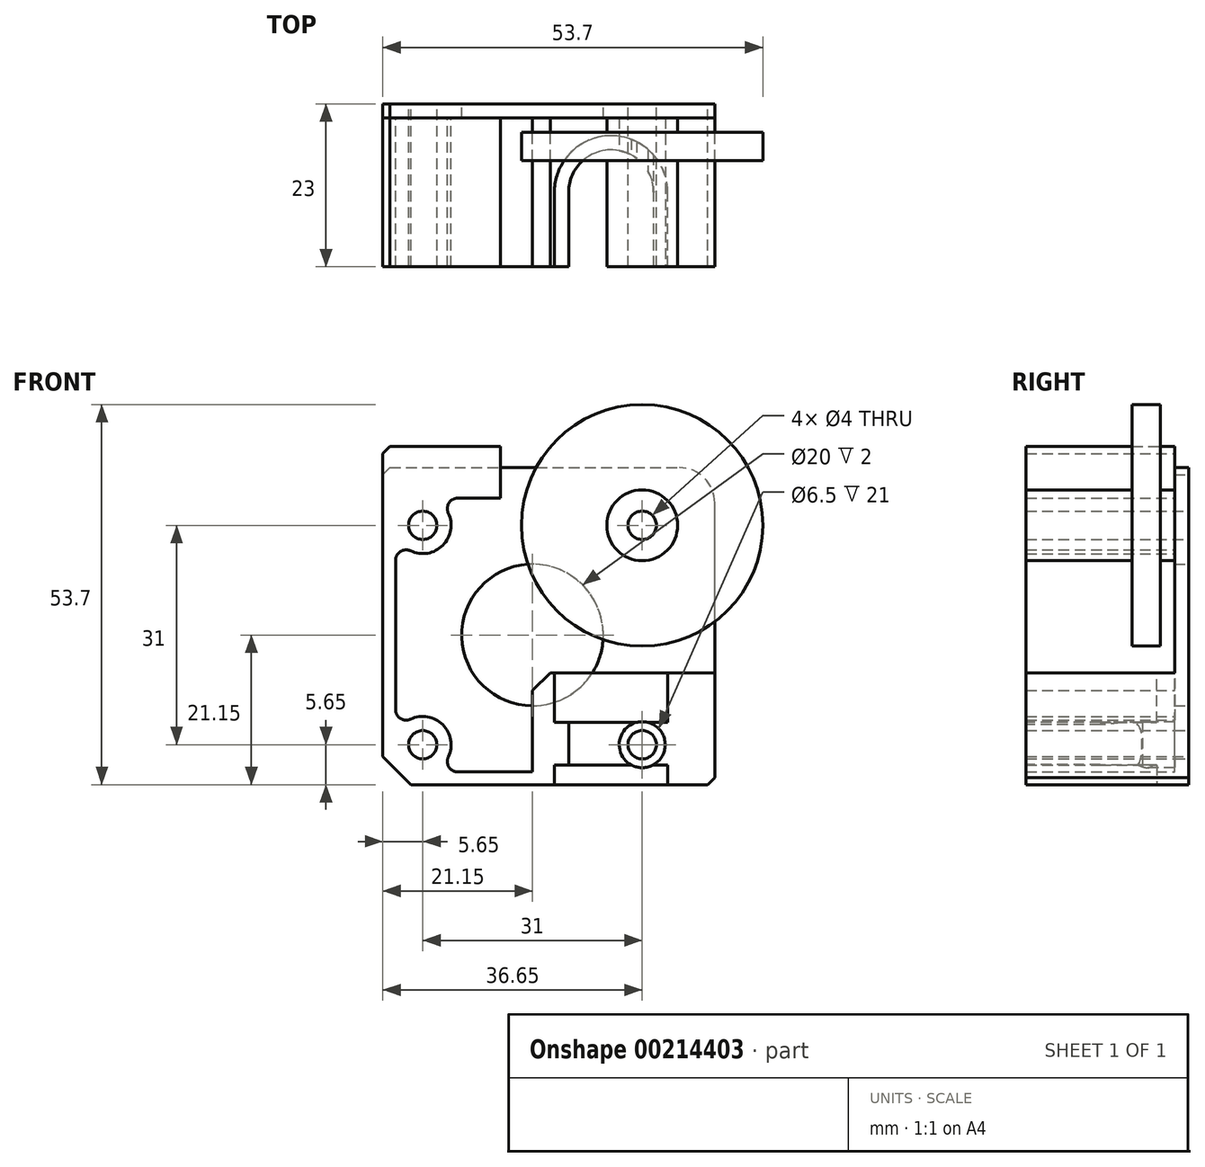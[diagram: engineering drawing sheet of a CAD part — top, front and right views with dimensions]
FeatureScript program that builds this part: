
annotation { "Feature Type Name" : "Feature", "Feature Type Description" : "" }
export const myFeature = defineFeature(function(context is Context, id is Id, definition is map)
    precondition{}
    {
        {
            var Q0;
            Q0=qCreatedBy(makeId("Front.planeOp"),FACE);
            var sketch = newSketch(context, id + "F0", { "sketchPlane" : qUnion([Q0])});
            skLineSegment(sketch, "E0.bottom", {"start": v(4, 0) * mm, "end": v(45.9, 0) * mm});
            skLineSegment(sketch, "E0.top", {"start": v(1, 44.8) * mm, "end": v(41.9, 44.8) * mm});
            skLineSegment(sketch, "E0.left", {"start": v(0, 4) * mm, "end": v(0, 43.8) * mm});
            skLineSegment(sketch, "E0.right", {"start": v(46.9, 1) * mm, "end": v(46.9, 39.8) * mm});
            skLineSegment(sketch, "E1.bottom", {"start": v(4, 0) * mm, "end": v(42.3, 0) * mm, "construction": true});
            skLineSegment(sketch, "E1.top", {"start": v(0, 42.3) * mm, "end": v(42.3, 42.3) * mm, "construction": true});
            skLineSegment(sketch, "E1.left", {"start": v(0, 4) * mm, "end": v(0, 42.3) * mm, "construction": true});
            skLineSegment(sketch, "E1.right", {"start": v(42.3, 0) * mm, "end": v(42.3, 42.3) * mm, "construction": true});
            skLineSegment(sketch, "E2", {"start": v(0, 0) * mm, "end": v(42.3, 42.3) * mm, "construction": true});
            skCircle(sketch, "E3", {"center": v(21.15, 21.15) * mm, "radius": 10 * mm});
            skLineSegment(sketch, "E4", {"start": v(21.15, 42.3) * mm, "end": v(21.15, 0) * mm, "construction": true});
            skCircle(sketch, "E5", {"center": v(36.65, 36.65) * mm, "radius": 2 * mm});
            skCircle(sketch, "E6", {"center": v(5.65, 5.65) * mm, "radius": 2 * mm});
            skLineSegment(sketch, "E7", {"start": v(0, 42.3) * mm, "end": v(42.3, 0) * mm, "construction": true});
            skCircle(sketch, "E8", {"center": v(5.65, 36.65) * mm, "radius": 2 * mm});
            skCircle(sketch, "E9", {"center": v(36.65, 5.65) * mm, "radius": 2 * mm});
            skLineSegment(sketch, "E10", {"start": v(0, 4) * mm, "end": v(4, 0) * mm});
            skLineSegment(sketch, "E11", {"start": v(0, 43.8) * mm, "end": v(1, 44.8) * mm});
            skLineSegment(sketch, "E12", {"start": v(45.9, 0) * mm, "end": v(46.9, 1) * mm});
            skPoint(sketch, "E13.visualSharp", {"position": v(46.9, 44.8) * mm});
            skArc(sketch, "E13.filletArc", {"start": v(46.9, 39.8) * mm, "mid": v(45.44, 43.34) * mm, "end": v(41.9, 44.8) * mm});
            skSolve(sketch);
        }
        {
            var Q0;
            Q0 = qSketchRegion(id + "F0", true);
            extrude(context, id + "F1", {"entities" : qUnion([Q0]), "depth" : 2 * mm});
        }
        {
            var Q0;
            Q0=makeQuery(id+"F1.opExtrude","CAP_FACE",FACE,{"disambiguationData":[OSD([sQuery(id+"F0.wireOp",EDGE,"E0.bottom"),sQuery(id+"F0.wireOp",EDGE,"E0.top"),sQuery(id+"F0.wireOp",EDGE,"E0.left"),sQuery(id+"F0.wireOp",EDGE,"E0.right"),sQuery(id+"F0.wireOp",EDGE,"E3"),sQuery(id+"F0.wireOp",EDGE,"E5"),sQuery(id+"F0.wireOp",EDGE,"E6"),sQuery(id+"F0.wireOp",EDGE,"E8"),sQuery(id+"F0.wireOp",EDGE,"E9"),sQuery(id+"F0.wireOp",EDGE,"E10"),sQuery(id+"F0.wireOp",EDGE,"E11"),sQuery(id+"F0.wireOp",EDGE,"E12"),sQuery(id+"F0.wireOp",EDGE,"E13.filletArc")])],"isStart":false});
            var sketch = newSketch(context, id + "F2", { "sketchPlane" : qUnion([Q0])});
            skLineSegment(sketch, "E14", {"start": v(0, 46.8) * mm, "end": v(0, 4) * mm});
            skLineSegment(sketch, "E15", {"start": v(0, 4) * mm, "end": v(4, 0) * mm});
            skArc(sketch, "E16", {"start": v(9.27, 3.94) * mm, "mid": v(8.48, 8.48) * mm, "end": v(3.94, 9.27) * mm});
            skLineSegment(sketch, "E17.1", {"start": v(10.62, 1.8) * mm, "end": v(21.15, 1.8) * mm});
            skLineSegment(sketch, "E18.trimOffspring", {"start": v(10.62, 40.5) * mm, "end": v(16.65, 40.5) * mm});
            skLineSegment(sketch, "E19.trimOffspring", {"start": v(1.8, 31.68) * mm, "end": v(1.8, 10.62) * mm});
            skArc(sketch, "E20.trimOffspring", {"start": v(3.94, 33.03) * mm, "mid": v(8.48, 33.82) * mm, "end": v(9.27, 38.36) * mm});
            skPoint(sketch, "E21.visualSharp", {"position": v(6.74, 1.8) * mm});
            skArc(sketch, "E21.filletArc", {"start": v(9.27, 3.94) * mm, "mid": v(9.36, 2.5) * mm, "end": v(10.62, 1.8) * mm});
            skPoint(sketch, "E22.visualSharp", {"position": v(1.8, 6.74) * mm});
            skArc(sketch, "E22.filletArc", {"start": v(1.8, 10.62) * mm, "mid": v(2.5, 9.36) * mm, "end": v(3.94, 9.27) * mm});
            skPoint(sketch, "E23.visualSharp", {"position": v(1.8, 35.56) * mm});
            skArc(sketch, "E23.filletArc", {"start": v(3.94, 33.03) * mm, "mid": v(2.5, 32.94) * mm, "end": v(1.8, 31.68) * mm});
            skPoint(sketch, "E24.visualSharp", {"position": v(6.74, 40.5) * mm});
            skArc(sketch, "E24.filletArc", {"start": v(10.62, 40.5) * mm, "mid": v(9.36, 39.8) * mm, "end": v(9.27, 38.36) * mm});
            skLineSegment(sketch, "E25", {"start": v(21.15, 1.8) * mm, "end": v(21.15, 13.3) * mm});
            skLineSegment(sketch, "E26", {"start": v(23.65, 15.8) * mm, "end": v(46.9, 15.8) * mm});
            skLineSegment(sketch, "E27", {"start": v(4, 0) * mm, "end": v(45.9, 0) * mm});
            skLineSegment(sketch, "E28", {"start": v(45.9, 0) * mm, "end": v(46.9, 1) * mm});
            skLineSegment(sketch, "E29", {"start": v(46.9, 1) * mm, "end": v(46.9, 15.8) * mm});
            skLineSegment(sketch, "E30", {"start": v(21.15, 13.3) * mm, "end": v(23.65, 15.8) * mm});
            skLineSegment(sketch, "E31", {"start": v(21.15, 13.3) * mm, "end": v(21.15, 21.15) * mm, "construction": true});
            skLineSegment(sketch, "E32", {"start": v(16.65, 47.8) * mm, "end": v(16.65, 40.5) * mm});
            skCircle(sketch, "E33", {"center": v(5.65, 36.65) * mm, "radius": 2 * mm});
            skCircle(sketch, "E34", {"center": v(5.65, 5.65) * mm, "radius": 2 * mm});
            skCircle(sketch, "E35", {"center": v(36.65, 5.65) * mm, "radius": 2 * mm});
            skLineSegment(sketch, "E36", {"start": v(0, 46.8) * mm, "end": v(1, 47.8) * mm});
            skLineSegment(sketch, "E37", {"start": v(1, 47.8) * mm, "end": v(16.65, 47.8) * mm});
            skSolve(sketch);
        }
        {
            var Q0;
            Q0 = qSketchRegion(id + "F2", true);
            extrude(context, id + "F3", {"entities" : qUnion([Q0]), "operationType" : NewBodyOperationType.ADD, "depth" : 21 * mm});
        }
        {
            var Q0;
            Q0=makeQuery(id+"F3.opExtrude","SWEPT_FACE",FACE,{"disambiguationData":[OSD([sQuery(id+"F2.wireOp",EDGE,"E26")])]});
            var sketch = newSketch(context, id + "F4", { "sketchPlane" : qUnion([Q0])});
            skArc(sketch, "E38", {"start": v(38.25, -12.5) * mm, "mid": v(32.25, -6.5) * mm, "end": v(26.25, -12.5) * mm});
            skLineSegment(sketch, "E39", {"start": v(26.25, -12.5) * mm, "end": v(26.25, -27.5) * mm});
            skLineSegment(sketch, "E40", {"start": v(26.25, -27.5) * mm, "end": v(38.25, -27.5) * mm});
            skLineSegment(sketch, "E41", {"start": v(38.25, -27.5) * mm, "end": v(38.25, -12.5) * mm});
            skSolve(sketch);
        }
        {
            var Q0;
            Q0 = qSketchRegion(id + "F4", true);
            extrude(context, id + "F5", {"entities" : qUnion([Q0]), "operationType" : NewBodyOperationType.REMOVE, "endBound" : BoundingType.THROUGH_ALL, "oppositeDirection" : true, "depth" : 25 * mm});
        }
        {
            var Q0;
            Q0=makeQuery(id+"F3.opExtrude","SWEPT_FACE",FACE,{"disambiguationData":[OSD([sQuery(id+"F2.wireOp",EDGE,"E26")])]});
            var sketch = newSketch(context, id + "F6", { "sketchPlane" : qUnion([Q0])});
            skArc(sketch, "E42", {"start": v(40.25, -12.5) * mm, "mid": v(32.25, -4.5) * mm, "end": v(24.25, -12.5) * mm});
            skLineSegment(sketch, "E43", {"start": v(24.25, -12.5) * mm, "end": v(24.25, -27.5) * mm});
            skLineSegment(sketch, "E44", {"start": v(24.25, -27.5) * mm, "end": v(40.25, -27.5) * mm});
            skLineSegment(sketch, "E45", {"start": v(40.25, -27.5) * mm, "end": v(40.25, -12.5) * mm});
            skSolve(sketch);
        }
        {
            var Q0;
            Q0 = qSketchRegion(id + "F6", true);
            extrude(context, id + "F7", {"entities" : qUnion([Q0]), "operationType" : NewBodyOperationType.REMOVE, "oppositeDirection" : true, "depth" : 7 * mm});
        }
        {
            var Q0;
            Q0=makeQuery(id+"F3.boolean.opBoolean","MERGE",FACE,{"derivedFrom":[makeQuery(id+"F1.opExtrude","SWEPT_FACE",FACE,{"disambiguationData":[OSD([sQuery(id+"F0.wireOp",EDGE,"E0.bottom")])]}),makeQuery(id+"F3.opExtrude","SWEPT_FACE",FACE,{"disambiguationData":[OSD([sQuery(id+"F2.wireOp",EDGE,"E27")])]})]});
            var sketch = newSketch(context, id + "F8", { "sketchPlane" : qUnion([Q0])});
            skArc(sketch, "E46", {"start": v(24.25, 12.5) * mm, "mid": v(32.25, 4.5) * mm, "end": v(40.25, 12.5) * mm});
            skLineSegment(sketch, "E47", {"start": v(24.25, 12.5) * mm, "end": v(24.25, 27.5) * mm});
            skLineSegment(sketch, "E48", {"start": v(24.25, 27.5) * mm, "end": v(40.25, 27.5) * mm});
            skLineSegment(sketch, "E49", {"start": v(40.25, 27.5) * mm, "end": v(40.25, 12.5) * mm});
            skSolve(sketch);
        }
        {
            var Q0;
            Q0 = qSketchRegion(id + "F8", true);
            extrude(context, id + "F9", {"entities" : qUnion([Q0]), "operationType" : NewBodyOperationType.REMOVE, "oppositeDirection" : true, "depth" : 2.8 * mm});
        }
        {
            var Q0;
            Q0=makeQuery(id+"F1.opExtrude","CAP_FACE",FACE,{"disambiguationData":[OSD([sQuery(id+"F0.wireOp",EDGE,"E0.bottom"),sQuery(id+"F0.wireOp",EDGE,"E0.top"),sQuery(id+"F0.wireOp",EDGE,"E0.left"),sQuery(id+"F0.wireOp",EDGE,"E0.right"),sQuery(id+"F0.wireOp",EDGE,"E3"),sQuery(id+"F0.wireOp",EDGE,"E5"),sQuery(id+"F0.wireOp",EDGE,"E6"),sQuery(id+"F0.wireOp",EDGE,"E8"),sQuery(id+"F0.wireOp",EDGE,"E9"),sQuery(id+"F0.wireOp",EDGE,"E10"),sQuery(id+"F0.wireOp",EDGE,"E11"),sQuery(id+"F0.wireOp",EDGE,"E12"),sQuery(id+"F0.wireOp",EDGE,"E13.filletArc")])],"isStart":false});
            var sketch = newSketch(context, id + "F10", { "sketchPlane" : qUnion([Q0])});
            skCircle(sketch, "E50", {"center": v(36.65, 36.65) * mm, "radius": 5 * mm});
            skCircle(sketch, "E51", {"center": v(36.65, 36.65) * mm, "radius": 2 * mm});
            skSolve(sketch);
        }
        {
            var Q0;
            Q0 = qSketchRegion(id + "F10", true);
            extrude(context, id + "F11", {"entities" : qUnion([Q0]), "operationType" : NewBodyOperationType.ADD, "depth" : 2 * mm});
        }
        {
            var Q0;
            Q0=makeQuery(id+"F11.opExtrude","CAP_FACE",FACE,{"disambiguationData":[OSD([sQuery(id+"F10.wireOp",EDGE,"E50"),sQuery(id+"F10.wireOp",EDGE,"E51")])],"isStart":false});
            var sketch = newSketch(context, id + "F12", { "sketchPlane" : qUnion([Q0])});
            skCircle(sketch, "E52", {"center": v(36.65, 36.65) * mm, "radius": 17.05 * mm});
            skCircle(sketch, "E53", {"center": v(36.65, 36.65) * mm, "radius": 2 * mm});
            skSolve(sketch);
        }
        {
            var Q0;
            Q0 = qSketchRegion(id + "F12", true);
            extrude(context, id + "F13", {"entities" : qUnion([Q0]), "operationType" : NewBodyOperationType.ADD, "depth" : 4 * mm});
        }
        {
            var Q0;
            Q0=makeQuery(id+"F13.opExtrude","CAP_FACE",FACE,{"disambiguationData":[OSD([sQuery(id+"F12.wireOp",EDGE,"E52"),sQuery(id+"F12.wireOp",EDGE,"E53")])],"isStart":false});
            var sketch = newSketch(context, id + "F14", { "sketchPlane" : qUnion([Q0])});
            skCircle(sketch, "E54", {"center": v(36.65, 36.65) * mm, "radius": 5 * mm});
            skCircle(sketch, "E55", {"center": v(36.65, 36.65) * mm, "radius": 2 * mm});
            skSolve(sketch);
        }
        {
            var Q0;
            Q0 = qSketchRegion(id + "F14", true);
            extrude(context, id + "F15", {"entities" : qUnion([Q0]), "operationType" : NewBodyOperationType.ADD, "depth" : 15 * mm});
        }
        {
            var Q0;
            {var subQ0=sQuery(id+"F2.wireOp",EDGE,"E29");var subQ1=sQuery(id+"F2.wireOp",EDGE,"E26");var subQ2=sQuery(id+"F2.wireOp",EDGE,"E27");var subQ3=sQuery(id+"F2.wireOp",EDGE,"E28");var subQ4=sQuery(id+"F2.wireOp",EDGE,"E35");Q0=makeQuery(id+"F5.boolean.opBoolean","SPLIT",FACE,{"disambiguationData":[TD([makeQuery(id+"F1.opExtrude","SWEPT_FACE",FACE,{"disambiguationData":[OSD([sQuery(id+"F0.wireOp",EDGE,"E0.right")])]})])],"derivedFrom":makeQuery(id+"F3.opExtrude","CAP_FACE",FACE,{"disambiguationData":[OSD([sQuery(id+"F2.wireOp",EDGE,"E14"),sQuery(id+"F2.wireOp",EDGE,"E15"),sQuery(id+"F2.wireOp",EDGE,"E16"),sQuery(id+"F2.wireOp",EDGE,"E17.1"),sQuery(id+"F2.wireOp",EDGE,"E18.trimOffspring"),sQuery(id+"F2.wireOp",EDGE,"E19.trimOffspring"),sQuery(id+"F2.wireOp",EDGE,"E20.trimOffspring"),sQuery(id+"F2.wireOp",EDGE,"E21.filletArc"),sQuery(id+"F2.wireOp",EDGE,"E22.filletArc"),sQuery(id+"F2.wireOp",EDGE,"E23.filletArc"),sQuery(id+"F2.wireOp",EDGE,"E24.filletArc"),sQuery(id+"F2.wireOp",EDGE,"E25"),subQ1,subQ2,subQ3,subQ0,sQuery(id+"F2.wireOp",EDGE,"E30"),sQuery(id+"F2.wireOp",EDGE,"E32"),sQuery(id+"F2.wireOp",EDGE,"E33"),sQuery(id+"F2.wireOp",EDGE,"E34"),subQ4,sQuery(id+"F2.wireOp",EDGE,"E36"),sQuery(id+"F2.wireOp",EDGE,"E37")])],"isStart":false})});}
            var sketch = newSketch(context, id + "F16", { "sketchPlane" : qUnion([Q0])});
            skCircle(sketch, "E56", {"center": v(36.65, 5.65) * mm, "radius": 3.25 * mm});
            skSolve(sketch);
        }
        {
            var Q0;
            Q0 = qSketchRegion(id + "F16", true);
            extrude(context, id + "F17", {"entities" : qUnion([Q0]), "operationType" : NewBodyOperationType.REMOVE, "oppositeDirection" : true, "depth" : 21 * mm});
        }
    });
